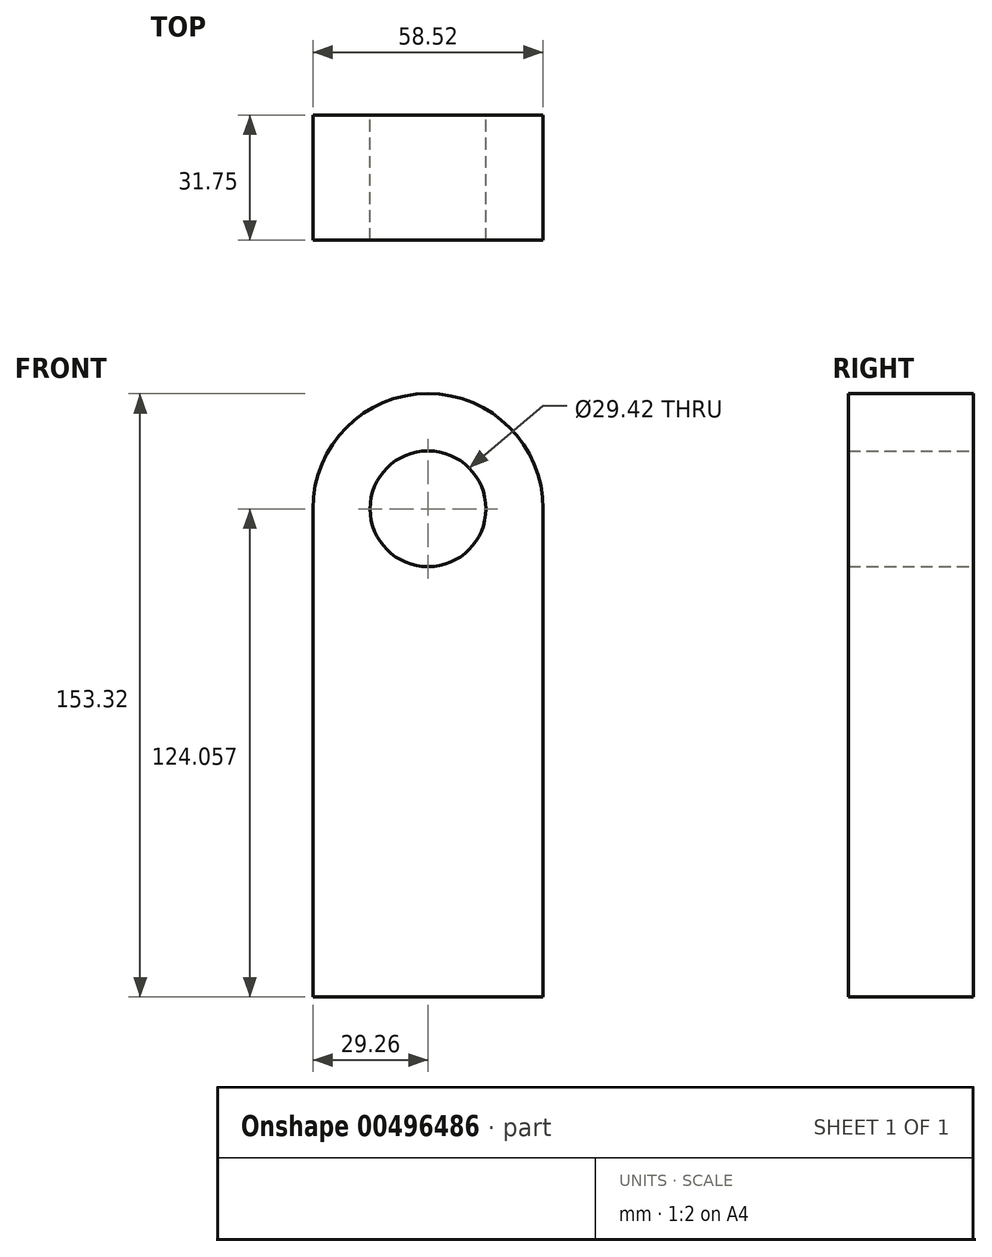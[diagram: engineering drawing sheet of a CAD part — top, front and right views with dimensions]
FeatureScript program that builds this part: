
annotation { "Feature Type Name" : "Feature", "Feature Type Description" : "" }
export const myFeature = defineFeature(function(context is Context, id is Id, definition is map)
    precondition{}
    {
        {
            var Q0;
            Q0=qCreatedBy(makeId("Front.planeOp"),FACE);
            var sketch = newSketch(context, id + "F0", { "sketchPlane" : qUnion([Q0])});
            skLineSegment(sketch, "E0.bottom", {"start": v(29.26, -62.03) * mm, "end": v(-29.26, -62.03) * mm});
            skLineSegment(sketch, "E0.left", {"start": v(29.26, -62.03) * mm, "end": v(29.26, 62.03) * mm});
            skLineSegment(sketch, "E0.right", {"start": v(-29.26, -62.03) * mm, "end": v(-29.26, 62.03) * mm});
            skPoint(sketch, "E0.middle", {"position": v(0, 0) * mm});
            skCircle(sketch, "E1", {"center": v(0, 62.03) * mm, "radius": 14.7 * mm});
            skArc(sketch, "E2", {"start": v(29.26, 62.03) * mm, "mid": v(0, 91.29) * mm, "end": v(-29.26, 62.03) * mm});
            skSolve(sketch);
        }
        {
            var Q0;
            Q0=makeQuery(id+"F0.imprint","IMPRINT",FACE,{"disambiguationData":[TD([[makeQuery(id+"F0.imprint","IMPRINT",EDGE,{"derivedFrom":sQuery(id+"F0.wireOp",EDGE,"E0.bottom")}),-1.0]])]});
            extrude(context, id + "F1", {"entities" : qUnion([Q0]), "depth" : 31.75 * mm});
        }
    });
